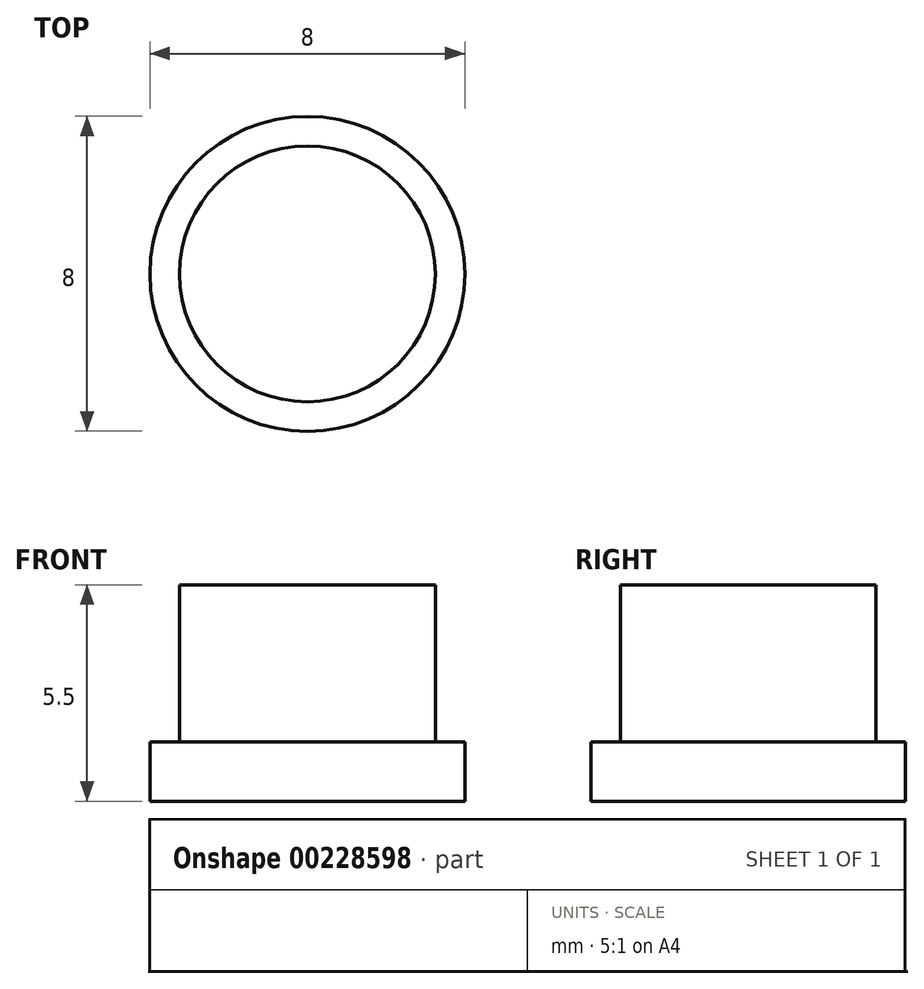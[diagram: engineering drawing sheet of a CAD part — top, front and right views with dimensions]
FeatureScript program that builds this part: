
annotation { "Feature Type Name" : "Feature", "Feature Type Description" : "" }
export const myFeature = defineFeature(function(context is Context, id is Id, definition is map)
    precondition{}
    {
        {
            var Q0;
            Q0=qCreatedBy(makeId("Top.planeOp"),FACE);
            var sketch = newSketch(context, id + "F0", { "sketchPlane" : qUnion([Q0])});
            skCircle(sketch, "E0", {"center": v(-19.5, 22.78) * mm, "radius": 4 * mm});
            skSolve(sketch);
        }
        {
            var Q0;
            Q0=makeQuery(id+"F0.imprint","IMPRINT",FACE,{"disambiguationData":[TD([[makeQuery(id+"F0.imprint","IMPRINT",EDGE,{"derivedFrom":sQuery(id+"F0.wireOp",EDGE,"E0")}),1.0]])]});
            extrude(context, id + "F1", {"entities" : qUnion([Q0]), "depth" : 1.5 * mm});
        }
        {
            var Q0;
            Q0=makeQuery(id+"F1.opExtrude","CAP_FACE",FACE,{"disambiguationData":[OSD([sQuery(id+"F0.wireOp",EDGE,"E0")])],"isStart":false});
            var sketch = newSketch(context, id + "F2", { "sketchPlane" : qUnion([Q0])});
            skCircle(sketch, "E1", {"center": v(-19.5, 22.78) * mm, "radius": 4 * mm, "construction": true});
            skPoint(sketch, "E1.first.point", {"position": v(-22.25, 25.68) * mm});
            skPoint(sketch, "E1.second.point", {"position": v(-16.43, 25.34) * mm});
            skPoint(sketch, "E1.third.point", {"position": v(-20.06, 18.82) * mm});
            skCircle(sketch, "E2", {"center": v(-19.5, 22.78) * mm, "radius": 3.25 * mm});
            skSolve(sketch);
        }
        {
            var Q0;
            Q0=makeQuery(id+"F2.imprint","IMPRINT",FACE,{"disambiguationData":[TD([[makeQuery(id+"F2.imprint","IMPRINT",EDGE,{"derivedFrom":sQuery(id+"F2.wireOp",EDGE,"E2")}),1.0]])]});
            extrude(context, id + "F3", {"entities" : qUnion([Q0]), "operationType" : NewBodyOperationType.ADD, "depth" : 4 * mm});
        }
    });
